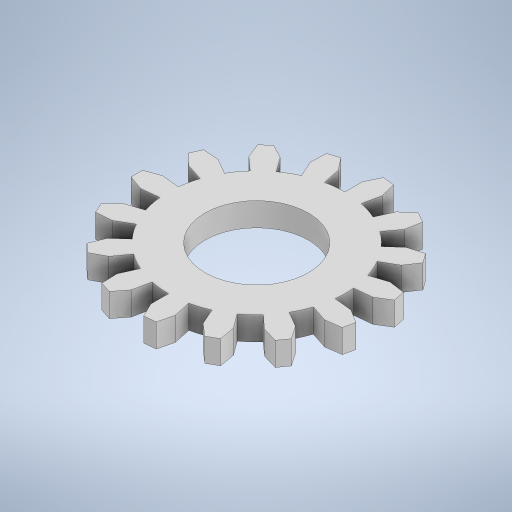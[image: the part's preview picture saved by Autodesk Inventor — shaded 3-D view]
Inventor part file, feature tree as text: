
AUTODESK INVENTOR PART (.ipt)
format: ipt  version: 2024.1 (Build 281209000, 209)  size: 389,632 bytes
history: native  units: mm
features: other x1, extrude x1, sketch x1
ambient origin geometry x8: Origin, YZ Plane, XZ Plane, XY Plane, X Axis, Y Axis, Z Axis, Center Point
bodies: Body1 (feature_tree)
feature tree (3):
  other  "ソリッド1"
  extrude  "押し出し1"  Depth=45.0mm
  sketch  "スケッチ1"
